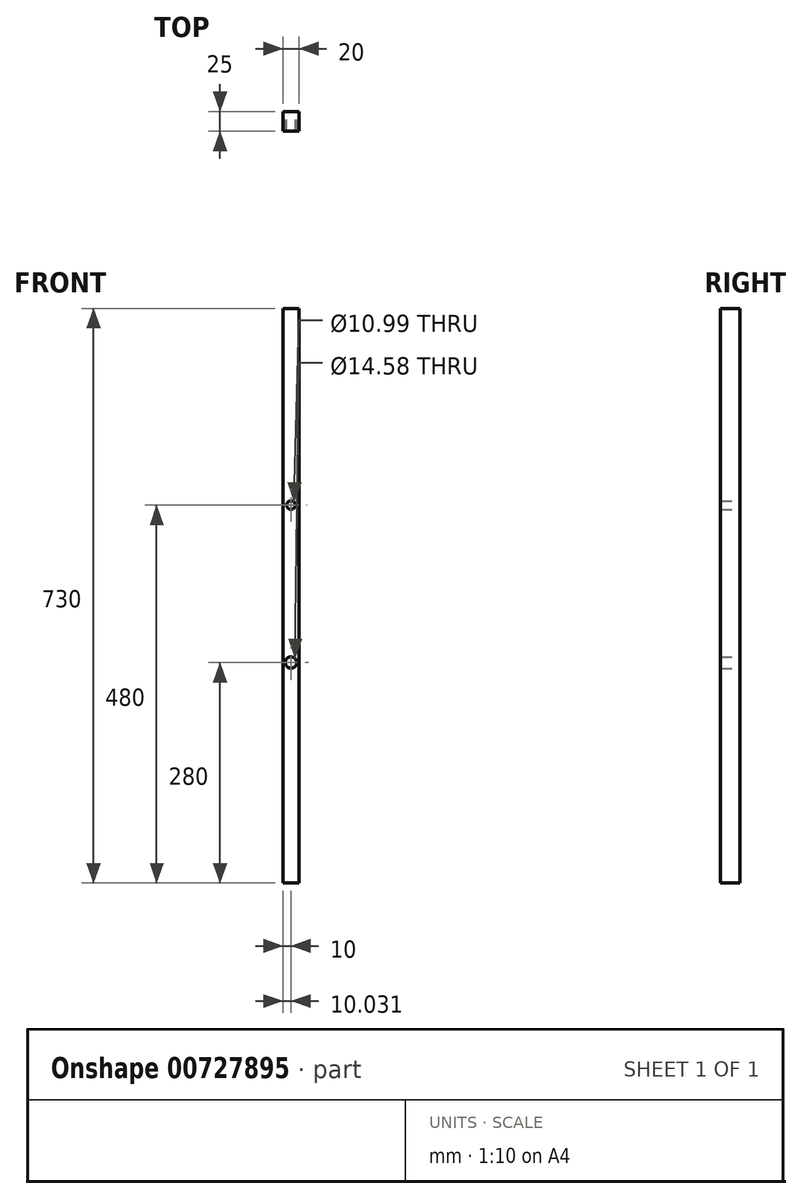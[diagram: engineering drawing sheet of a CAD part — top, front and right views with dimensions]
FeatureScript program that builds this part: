
annotation { "Feature Type Name" : "Feature", "Feature Type Description" : "" }
export const myFeature = defineFeature(function(context is Context, id is Id, definition is map)
    precondition{}
    {
        {
            var Q0;
            Q0=qCreatedBy(makeId("Front.planeOp"),FACE);
            var sketch = newSketch(context, id + "F0", { "sketchPlane" : qUnion([Q0])});
            skLineSegment(sketch, "E0.bottom", {"start": v(0, -286.52) * mm, "end": v(-20, -286.52) * mm});
            skLineSegment(sketch, "E0.top", {"start": v(0, 443.48) * mm, "end": v(-20, 443.48) * mm});
            skLineSegment(sketch, "E0.left", {"start": v(0, -286.52) * mm, "end": v(0, 443.48) * mm});
            skLineSegment(sketch, "E0.right", {"start": v(-20, -286.52) * mm, "end": v(-20, 443.48) * mm});
            skPoint(sketch, "E0.middle", {"position": v(-10, 78.48) * mm});
            skCircle(sketch, "E1", {"center": v(-9.97, 193.48) * mm, "radius": 5.5 * mm});
            skCircle(sketch, "E2", {"center": v(-10, -6.52) * mm, "radius": 7.29 * mm});
            skSolve(sketch);
        }
        {
            var Q0;
            Q0 = qSketchRegion(id + "F0", true);
            extrude(context, id + "F1", {"entities" : qUnion([Q0]), "depth" : 25 * mm, "offsetDistance" : 25 * mm});
        }
    });
